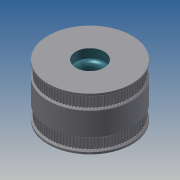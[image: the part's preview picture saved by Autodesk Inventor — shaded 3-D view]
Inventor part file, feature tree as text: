
AUTODESK INVENTOR PART (.ipt)
format: ipt  version: 2013 (Build 170138000, 138)  size: 813,056 bytes
history: native  units: mm
features: extrude x4, sketch x4, other x3, fillet x2
ambient origin geometry x8: Origin, YZ Plane, XZ Plane, XY Plane, X Axis, Y Axis, Z Axis, Center Point
bodies: Solid1 (feature_tree)
feature tree (13):
  other  "z idler pulley 2.iam"
  other  "100 pulley blank.ipt:1"
  other  "100 pulley blank.ipt:2"
  extrude  "Extrusion1"  Depth=10.0mm TaperAngle=0.0deg
  extrude  "Extrusion2"  Depth=10.0mm TaperAngle=0.0deg
  extrude  "Extrusion3"  Depth=7.0mm TaperAngle=0.0deg
  extrude  "Extrusion4"  Depth=7.0mm TaperAngle=0.0deg
  fillet  "Fillet1"  Radius=3.5mm
  fillet  "Fillet2"  Radius=3.5mm
  sketch  "Sketch1"  dims[d0=10.0mm d1=10.0mm d2=0.0mm]
  sketch  "Sketch2"  dims[d3=15.0mm d5=10.0mm d6=0.0mm]
  sketch  "Sketch3"  dims[d7=22.0mm d9=7.0mm d10=0.0mm]
  sketch  "Sketch4"  dims[d11=22.0mm d13=7.0mm d14=0.0mm d15=3.5mm d16=3.5mm]
